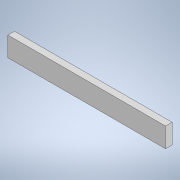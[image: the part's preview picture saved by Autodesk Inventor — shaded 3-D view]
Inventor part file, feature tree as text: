
AUTODESK INVENTOR PART (.ipt)
format: ipt  version: 2021 (Build 250183000, 183)  size: 124,928 bytes
history: native  units: in
note: dims shown in document units (in); Inventor stores cm internally (conversion verified against a paired STEP export)
features: extrude x2, sketch x2, pattern_linear x1, projected_geometry x1
ambient origin geometry x8: Origin, YZ Plane, XZ Plane, XY Plane, X Axis, Y Axis, Z Axis, Center Point
bodies: Solid1 (feature_tree)
feature tree (6):
  extrude  "Extrusion1"  Depth=0.375in
  extrude  "Extrusion2"  Depth=0.125in
  pattern_linear  "Rectangular Pattern1"  Spacing1=0.082in  [1 undecoded]
  sketch  "Sketch1"  dims[d0=3.0in d1=0.375in]
  sketch  "Sketch2"  dims[d2=0.125in d3=0.0in d4=0.125in d5=0.082in d6=0.0312in d7=0.0in d8=4.3307in d10=0.25in]
  projected_geometry  "Projected Loop1"
note: 1 required parameter value undecoded (feature->parameter linkage not recoverable at this tier; creation-order binding heuristic only, values carry confidence <= 0.55)
